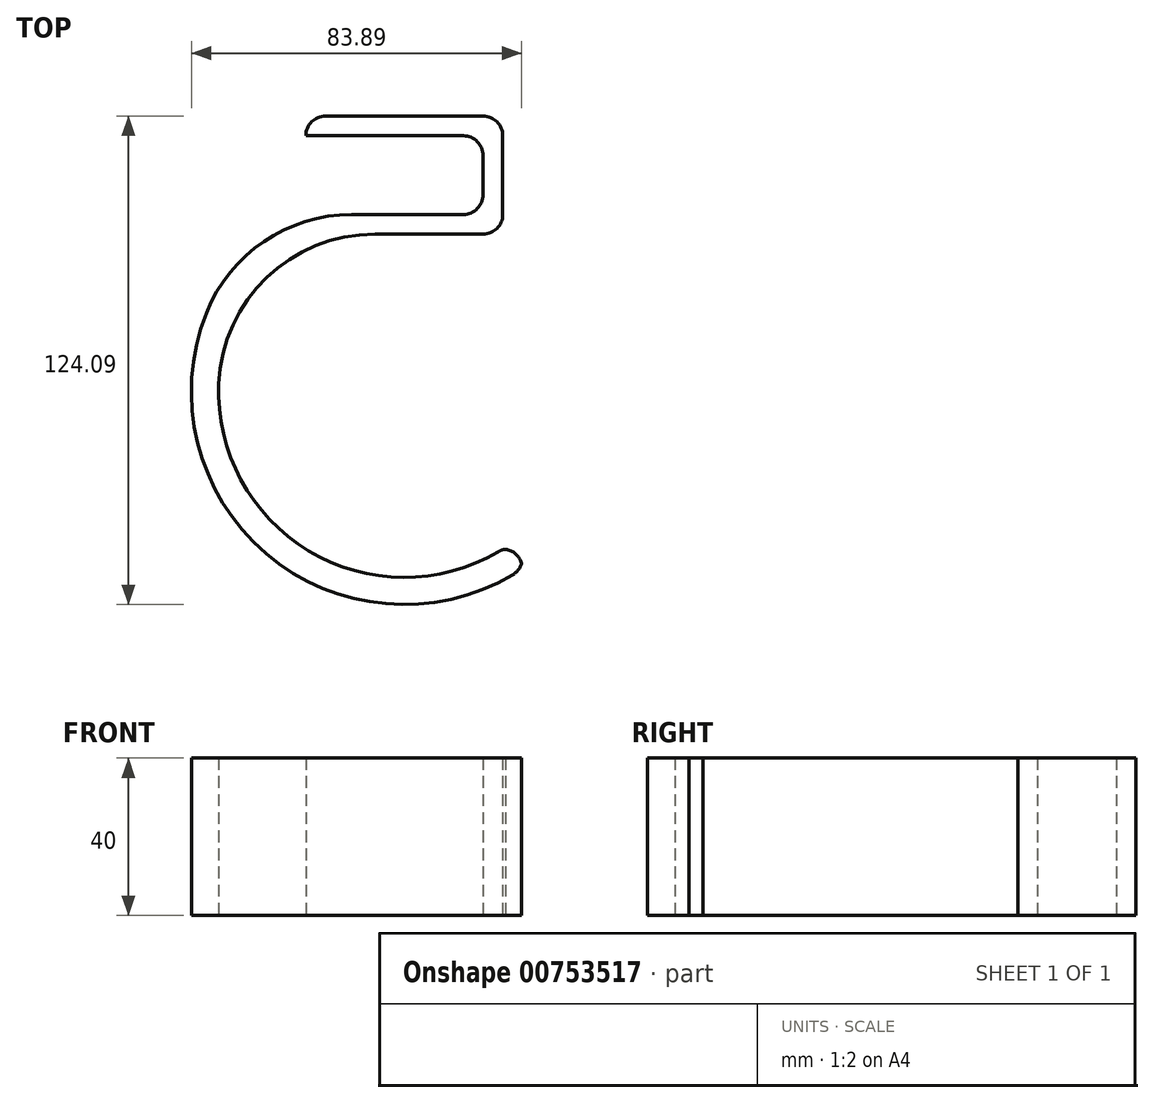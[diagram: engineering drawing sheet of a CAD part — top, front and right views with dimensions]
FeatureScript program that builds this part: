
annotation { "Feature Type Name" : "Feature", "Feature Type Description" : "" }
export const myFeature = defineFeature(function(context is Context, id is Id, definition is map)
    precondition{}
    {
        {
            var Q0;
            Q0=qCreatedBy(makeId("Top.planeOp"),FACE);
            var sketch = newSketch(context, id + "F0", { "sketchPlane" : qUnion([Q0])});
            skLineSegment(sketch, "E0.1.1.10", {"start": v(5, -9.23) * mm, "end": v(5, -14.23) * mm});
            skLineSegment(sketch, "E0.2.1.0", {"start": v(50, 10.77) * mm, "end": v(50, -9.23) * mm});
            skLineSegment(sketch, "E0.2.1.4", {"start": v(55, 15.77) * mm, "end": v(55, -14.23) * mm});
            skLineSegment(sketch, "E0.2.1.7", {"start": v(50, 15.77) * mm, "end": v(55, 15.77) * mm});
            skLineSegment(sketch, "E0.2.1.8", {"start": v(55, -14.23) * mm, "end": v(50, -14.23) * mm});
            skLineSegment(sketch, "E0.2.1.10", {"start": v(50, -9.23) * mm, "end": v(50, -14.23) * mm});
            skLineSegment(sketch, "E0.2.1.11", {"start": v(50, 10.77) * mm, "end": v(50, 15.77) * mm});
            skLineSegment(sketch, "E1", {"start": v(50, -9.23) * mm, "end": v(5, -9.23) * mm});
            skLineSegment(sketch, "E2", {"start": v(5, -14.23) * mm, "end": v(50, -14.23) * mm});
            skLineSegment(sketch, "E3", {"start": v(50, 10.77) * mm, "end": v(5, 10.77) * mm});
            skLineSegment(sketch, "E4", {"start": v(5, 10.77) * mm, "end": v(5, 15.77) * mm});
            skLineSegment(sketch, "E5", {"start": v(5, 15.77) * mm, "end": v(50, 15.77) * mm});
            skLineSegment(sketch, "E6", {"start": v(55, -94.23) * mm, "end": v(60, -94.23) * mm});
            skLineSegment(sketch, "E7", {"start": v(60, -94.23) * mm, "end": v(60, -99.23) * mm});
            skLineSegment(sketch, "E8", {"start": v(5, -9.23) * mm, "end": v(0, -9.23) * mm});
            skCircle(sketch, "E9", {"center": v(30, -54.23) * mm, "radius": 54.08 * mm});
            skCircle(sketch, "E10", {"center": v(30, -54.23) * mm, "radius": 47.17 * mm});
            skSolve(sketch);
        }
        {
            var Q0;
            Q0=makeQuery(id+"F0.imprint","IMPRINT",FACE,{"disambiguationData":[TD([[makeQuery(id+"F0.imprint","IMPRINT",EDGE,{"derivedFrom":sQuery(id+"F0.wireOp",EDGE,"E0.2.1.11")}),1.0]])]});
            var Q1;
            Q1=makeQuery(id+"F0.imprint","IMPRINT",FACE,{"disambiguationData":[TD([[makeQuery(id+"F0.imprint","IMPRINT",EDGE,{"derivedFrom":sQuery(id+"F0.wireOp",EDGE,"E0.2.1.0")}),1.0]])]});
            var Q2;
            Q2=makeQuery(id+"F0.imprint","IMPRINT",FACE,{"disambiguationData":[TD([[makeQuery(id+"F0.imprint","IMPRINT",EDGE,{"derivedFrom":sQuery(id+"F0.wireOp",EDGE,"E0.1.1.10")}),1.0]])]});
            var Q3;
            Q3=makeQuery(id+"F0.imprint","IMPRINT",FACE,{"disambiguationData":[TD([[makeQuery(id+"F0.imprint","IMPRINT",EDGE,{"derivedFrom":sQuery(id+"F0.wireOp",EDGE,"E0.1.1.10")}),-1.0]])]});
            var Q4;
            {var subQ6=sQuery(id+"F0.wireOp",EDGE,"E2");Q4=makeQuery(id+"F0.imprint","IMPRINT",FACE,{"disambiguationData":[TD([[makeQuery(id+"F0.imprint","IMPRINT",EDGE,{"derivedFrom":subQ6}),1.0]])]});}
            var Q5;
            {var subQ1=sQuery(id+"F0.wireOp",EDGE,"E0.2.1.10");var subQ3=sQuery(id+"F0.wireOp",EDGE,"E10");var subQ4=makeQuery(id+"F0.imprint","INTERSECT",VERTEX,{"derivedFrom":[subQ1,subQ3]});Q5=makeQuery(id+"F0.imprint","IMPRINT",FACE,{"disambiguationData":[TD([[makeQuery(id+"F0.imprint","IMPRINT",EDGE,{"disambiguationData":[TD([[subQ4,-1.0]])],"derivedFrom":subQ3}),-1.0]])]});}
            var Q6;
            {var subQ0=sQuery(id+"F0.wireOp",EDGE,"E0.2.1.8");Q6=makeQuery(id+"F0.imprint","IMPRINT",FACE,{"disambiguationData":[TD([[makeQuery(id+"F0.imprint","IMPRINT",EDGE,{"derivedFrom":subQ0}),-1.0]])]});}
            extrude(context, id + "F1", {"entities" : qUnion([Q0, Q1, Q2, Q3, Q4, Q5, Q6]), "depth" : 40 * mm, "offsetDistance" : 25 * mm});
        }
        {
            var Q0;
            Q0=makeQuery(id+"F1.opExtrude","SWEPT_EDGE",EDGE,{"disambiguationData":[OSD([sQuery(id+"F0.wireOp",EDGE,"E0.2.1.4"),sQuery(id+"F0.wireOp",EDGE,"E0.2.1.8")])]});
            var Q1;
            Q1=makeQuery(id+"F1.opExtrude","SWEPT_EDGE",EDGE,{"disambiguationData":[OSD([sQuery(id+"F0.wireOp",EDGE,"E0.2.1.4"),sQuery(id+"F0.wireOp",EDGE,"E0.2.1.7")])]});
            var Q2;
            Q2=makeQuery(id+"F1.opExtrude","SWEPT_EDGE",EDGE,{"disambiguationData":[OSD([sQuery(id+"F0.wireOp",EDGE,"E4"),sQuery(id+"F0.wireOp",EDGE,"E5")])]});
            var Q3;
            Q3=makeQuery(id+"F1.opExtrude","SWEPT_EDGE",EDGE,{"disambiguationData":[OSD([sQuery(id+"F0.wireOp",EDGE,"E0.2.1.0"),sQuery(id+"F0.wireOp",EDGE,"E0.2.1.10"),sQuery(id+"F0.wireOp",EDGE,"E1")])]});
            var Q4;
            Q4=makeQuery(id+"F1.opExtrude","SWEPT_EDGE",EDGE,{"disambiguationData":[OSD([sQuery(id+"F0.wireOp",EDGE,"E0.2.1.0"),sQuery(id+"F0.wireOp",EDGE,"E0.2.1.11"),sQuery(id+"F0.wireOp",EDGE,"E3")])]});
            var Q5;
            Q5=makeQuery(id+"F1.opExtrude","SWEPT_EDGE",EDGE,{"disambiguationData":[OSD([sQuery(id+"F0.wireOp",EDGE,"1VKRzm2R-rF6U-eRbp-6e8Z-sprnfeJABVeH"),sQuery(id+"F0.wireOp",EDGE,"E6")])]});
            var Q6;
            Q6=makeQuery(id+"F1.opExtrude","SWEPT_EDGE",EDGE,{"disambiguationData":[OSD([sQuery(id+"F0.wireOp",EDGE,"E6"),sQuery(id+"F0.wireOp",EDGE,"E7")])]});
            var Q7;
            Q7=makeQuery(id+"F1.opExtrude","SWEPT_EDGE",EDGE,{"disambiguationData":[OSD([sQuery(id+"F0.wireOp",EDGE,"E7"),sQuery(id+"F0.wireOp",EDGE,"1DFakgWC-PhlO-F0ZU-Goez-q4otgRwItFnK")])]});
            fillet(context, id + "F2", {"entities" : qUnion([Q0, Q1, Q2, Q3, Q4, Q5, Q6, Q7]), "radius" : 5 * mm, "tangentPropagation" : true, "allowEdgeOverflow" : false});
        }
        {
            var Q0;
            Q0=makeQuery(id+"F1.opExtrude","SWEPT_EDGE",EDGE,{"disambiguationData":[OSD([sQuery(id+"F0.wireOp",EDGE,"E8"),sQuery(id+"F0.wireOp",EDGE,"E9")])]});
            var Q1;
            Q1=makeQuery(id+"F1.opExtrude","SWEPT_EDGE",EDGE,{"disambiguationData":[OSD([sQuery(id+"F0.wireOp",EDGE,"E0.1.1.10"),sQuery(id+"F0.wireOp",EDGE,"E2"),sQuery(id+"F0.wireOp",EDGE,"E10")])]});
            fillet(context, id + "F3", {"entities" : qUnion([Q0, Q1]), "radius" : 39.69 * mm, "tangentPropagation" : true, "allowEdgeOverflow" : false});
        }
    });
